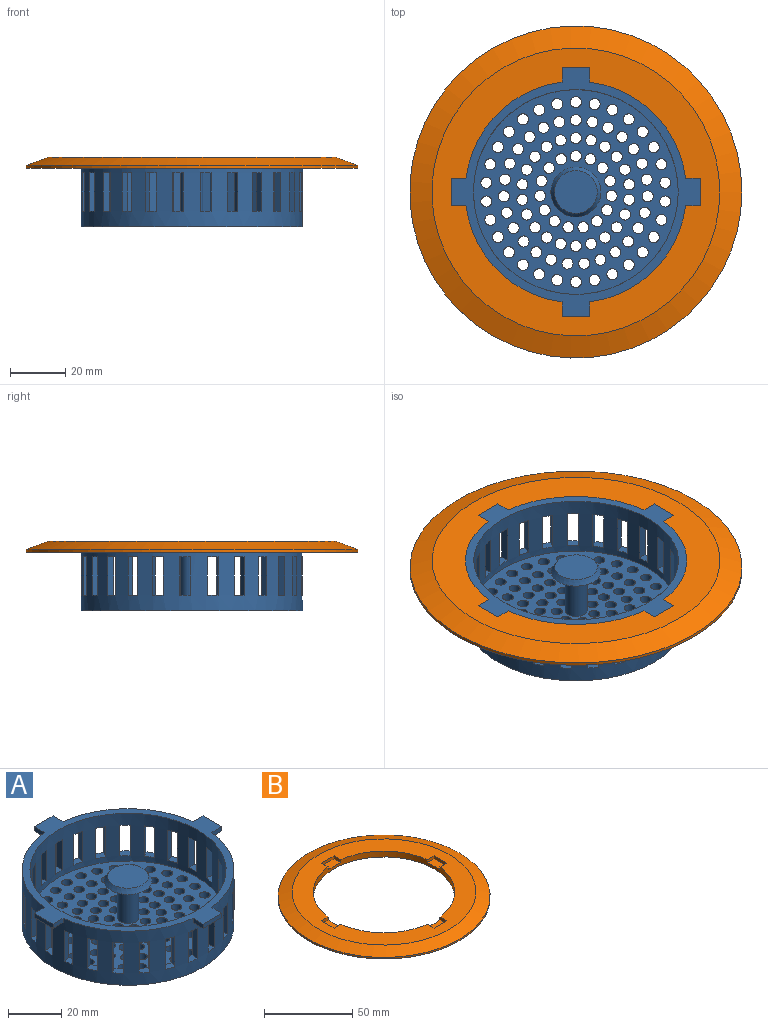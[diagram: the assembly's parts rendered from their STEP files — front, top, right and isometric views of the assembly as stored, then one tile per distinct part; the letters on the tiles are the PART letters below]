
ASSEMBLY  parts=2 mates=1
PART A: 226 faces, bbox 90x90x25 mm
  f0: cylinder r=40mm len=80mm, axis (0,0,-1), area 4802.4mm2, adj f2,f3,f5,f6,f8,f9,f10,f12
  f1: cylinder r=37mm len=74mm, axis (0,0,-1), area 3713.8mm2, adj f2,f4,f126,f127,f128,f129,f130,f131
  f2: plane 90x90mm, normal (0,0,1), area 929.9mm2, adj f0,f1,f5,f6,f7,f9,f10,f11
  f3: plane 80x80mm, normal (0,0,-1), area 3757.3mm2, adj f0,f21,f22,f23,f24,f25,f26,f27
  f4: plane 74x74mm, normal (0,0,1), area 2981.4mm2, adj f1,f21,f22,f23,f24,f25,f26,f27
  f5: plane 5.31x2mm, normal (-1,0,0), area 10.6mm2, adj f0,f2,f7,f8
  f6: plane 5.31x2mm, normal (1,0,0), area 10.6mm2, adj f0,f2,f7,f8
  f7: plane 10x2mm, normal (0,1,0), area 20mm2, adj f2,f5,f6,f8
  f8: plane 10x5.31mm, normal (0,0,-1), area 51mm2, adj f0,f5,f6,f7
  f9: plane 5.31x2mm, normal (0,-1,0), area 10.6mm2, adj f0,f2,f11,f12
  f10: plane 5.31x2mm, normal (0,1,0), area 10.6mm2, adj f0,f2,f11,f12
  f11: plane 10x2mm, normal (-1,0,0), area 20mm2, adj f2,f9,f10,f12
  f12: plane 10x5.31mm, normal (0,0,-1), area 51mm2, adj f0,f9,f10,f11
  f13: plane 5.31x2mm, normal (1,0,0), area 10.6mm2, adj f0,f2,f15,f16
  f14: plane 5.31x2mm, normal (-1,0,0), area 10.6mm2, adj f0,f2,f15,f16
  f15: plane 10x2mm, normal (0,-1,0), area 20mm2, adj f2,f13,f14,f16
  f16: plane 10x5.31mm, normal (0,0,-1), area 51mm2, adj f0,f13,f14,f15
  f17: plane 5.31x2mm, normal (0,1,0), area 10.6mm2, adj f0,f2,f19,f20
  f18: plane 5.31x2mm, normal (0,-1,0), area 10.6mm2, adj f0,f2,f19,f20
  f19: plane 10x2mm, normal (1,0,0), area 20mm2, adj f2,f17,f18,f20
  f20: plane 10x5.31mm, normal (0,0,-1), area 51mm2, adj f0,f17,f18,f19
  f21: cylinder r=2mm len=4mm, axis (0,0,1), area 37.7mm2, adj f3,f4
  f22: cylinder r=2mm len=4mm, axis (0,0,1), area 37.7mm2, adj f3,f4
  f23: cylinder r=2mm len=4mm, axis (0,0,1), area 37.7mm2, adj f3,f4
  f24: cylinder r=2mm len=4mm, axis (0,0,1), area 37.7mm2, adj f3,f4
  f25: cylinder r=2mm len=4mm, axis (0,0,1), area 37.7mm2, adj f3,f4
  f26: cylinder r=2mm len=4mm, axis (0,0,1), area 37.7mm2, adj f3,f4
  f27: cylinder r=2mm len=4mm, axis (0,0,1), area 37.7mm2, adj f3,f4
  f28: cylinder r=2mm len=4mm, axis (0,0,1), area 37.7mm2, adj f3,f4
  f29: cylinder r=2mm len=4mm, axis (0,0,1), area 37.7mm2, adj f3,f4
  f30: cylinder r=2mm len=4mm, axis (0,0,1), area 37.7mm2, adj f3,f4
  f31: cylinder r=2mm len=4mm, axis (0,0,1), area 37.7mm2, adj f3,f4
  f32: cylinder r=2mm len=4mm, axis (0,0,1), area 37.7mm2, adj f3,f4
  f33: cylinder r=2mm len=4mm, axis (0,0,1), area 37.7mm2, adj f3,f4
  f34: cylinder r=2mm len=4mm, axis (0,0,1), area 37.7mm2, adj f3,f4
  f35: cylinder r=2mm len=4mm, axis (0,0,1), area 37.7mm2, adj f3,f4
  f36: cylinder r=2mm len=4mm, axis (0,0,1), area 37.7mm2, adj f3,f4
  f37: cylinder r=2mm len=4mm, axis (0,0,1), area 37.7mm2, adj f3,f4
  f38: cylinder r=2mm len=4mm, axis (0,0,1), area 37.7mm2, adj f3,f4
  f39: cylinder r=2mm len=4mm, axis (0,0,1), area 37.7mm2, adj f3,f4
  f40: cylinder r=2mm len=4mm, axis (0,0,1), area 37.7mm2, adj f3,f4
  f41: cylinder r=2mm len=4mm, axis (0,0,1), area 37.7mm2, adj f3,f4
  f42: cylinder r=2mm len=4mm, axis (0,0,1), area 37.7mm2, adj f3,f4
  f43: cylinder r=2mm len=4mm, axis (0,0,1), area 37.7mm2, adj f3,f4
  f44: cylinder r=2mm len=4mm, axis (0,0,1), area 37.7mm2, adj f3,f4
  f45: cylinder r=2mm len=4mm, axis (0,0,1), area 37.7mm2, adj f3,f4
  f46: cylinder r=2mm len=4mm, axis (0,0,1), area 37.7mm2, adj f3,f4
  f47: cylinder r=2mm len=4mm, axis (0,0,1), area 37.7mm2, adj f3,f4
  f48: cylinder r=2mm len=4mm, axis (0,0,1), area 37.7mm2, adj f3,f4
  f49: cylinder r=2mm len=4mm, axis (0,0,1), area 37.7mm2, adj f3,f4
  f50: cylinder r=2mm len=4mm, axis (0,0,1), area 37.7mm2, adj f3,f4
  f51: cylinder r=2mm len=4mm, axis (0,0,1), area 37.7mm2, adj f3,f4
  f52: cylinder r=2mm len=4mm, axis (0,0,1), area 37.7mm2, adj f3,f4
  f53: cylinder r=2mm len=4mm, axis (0,0,1), area 37.7mm2, adj f3,f4
  f54: cylinder r=2mm len=4mm, axis (0,0,1), area 37.7mm2, adj f3,f4
  f55: cylinder r=2mm len=4mm, axis (0,0,1), area 37.7mm2, adj f3,f4
  f56: cylinder r=2mm len=4mm, axis (0,0,1), area 37.7mm2, adj f3,f4
  f57: cylinder r=2mm len=4mm, axis (0,0,1), area 37.7mm2, adj f3,f4
  f58: cylinder r=2mm len=4mm, axis (0,0,1), area 37.7mm2, adj f3,f4
  f59: cylinder r=2mm len=4mm, axis (0,0,1), area 37.7mm2, adj f3,f4
  f60: cylinder r=2mm len=4mm, axis (0,0,1), area 37.7mm2, adj f3,f4
  f61: cylinder r=2mm len=4mm, axis (0,0,1), area 37.7mm2, adj f3,f4
  f62: cylinder r=2mm len=4mm, axis (0,0,1), area 37.7mm2, adj f3,f4
  f63: cylinder r=2mm len=4mm, axis (0,0,1), area 37.7mm2, adj f3,f4
  f64: cylinder r=2mm len=4mm, axis (0,0,1), area 37.7mm2, adj f3,f4
  f65: cylinder r=2mm len=4mm, axis (0,0,1), area 37.7mm2, adj f3,f4
  f66: cylinder r=2mm len=4mm, axis (0,0,1), area 37.7mm2, adj f3,f4
  f67: cylinder r=2mm len=4mm, axis (0,0,1), area 37.7mm2, adj f3,f4
  f68: cylinder r=2mm len=4mm, axis (0,0,1), area 37.7mm2, adj f3,f4
  f69: cylinder r=2mm len=4mm, axis (0,0,1), area 37.7mm2, adj f3,f4
  f70: cylinder r=2mm len=4mm, axis (0,0,1), area 37.7mm2, adj f3,f4
  f71: cylinder r=2mm len=4mm, axis (0,0,1), area 37.7mm2, adj f3,f4
  f72: cylinder r=2mm len=4mm, axis (0,0,1), area 37.7mm2, adj f3,f4
  f73: cylinder r=2mm len=4mm, axis (0,0,1), area 37.7mm2, adj f3,f4
  f74: cylinder r=2mm len=4mm, axis (0,0,1), area 37.7mm2, adj f3,f4
  f75: cylinder r=2mm len=4mm, axis (0,0,1), area 37.7mm2, adj f3,f4
  f76: cylinder r=2mm len=4mm, axis (0,0,1), area 37.7mm2, adj f3,f4
  f77: cylinder r=2mm len=4mm, axis (0,0,1), area 37.7mm2, adj f3,f4
  f78: cylinder r=2mm len=4mm, axis (0,0,1), area 37.7mm2, adj f3,f4
  f79: cylinder r=2mm len=4mm, axis (0,0,1), area 37.7mm2, adj f3,f4
  f80: cylinder r=2mm len=4mm, axis (0,0,1), area 37.7mm2, adj f3,f4
  f81: cylinder r=2mm len=4mm, axis (0,0,1), area 37.7mm2, adj f3,f4
  f82: cylinder r=2mm len=4mm, axis (0,0,1), area 37.7mm2, adj f3,f4
  f83: cylinder r=2mm len=4mm, axis (0,0,1), area 37.7mm2, adj f3,f4
  f84: cylinder r=2mm len=4mm, axis (0,0,1), area 37.7mm2, adj f3,f4
  f85: cylinder r=2mm len=4mm, axis (0,0,1), area 37.7mm2, adj f3,f4
  f86: cylinder r=2mm len=4mm, axis (0,0,1), area 37.7mm2, adj f3,f4
  f87: cylinder r=2mm len=4mm, axis (0,0,1), area 37.7mm2, adj f3,f4
  f88: cylinder r=2mm len=4mm, axis (0,0,1), area 37.7mm2, adj f3,f4
  f89: cylinder r=2mm len=4mm, axis (0,0,1), area 37.7mm2, adj f3,f4
  f90: cylinder r=2mm len=4mm, axis (0,0,1), area 37.7mm2, adj f3,f4
  f91: cylinder r=2mm len=4mm, axis (0,0,1), area 37.7mm2, adj f3,f4
  f92: cylinder r=2mm len=4mm, axis (0,0,1), area 37.7mm2, adj f3,f4
  f93: cylinder r=2mm len=4mm, axis (0,0,1), area 37.7mm2, adj f3,f4
  f94: cylinder r=2mm len=4mm, axis (0,0,1), area 37.7mm2, adj f3,f4
  f95: cylinder r=2mm len=4mm, axis (0,0,1), area 37.7mm2, adj f3,f4
  f96: cylinder r=2mm len=4mm, axis (0,0,1), area 37.7mm2, adj f3,f4
  f97: cylinder r=2mm len=4mm, axis (0,0,1), area 37.7mm2, adj f3,f4
  f98: cylinder r=2mm len=4mm, axis (0,0,1), area 37.7mm2, adj f3,f4
  f99: cylinder r=2mm len=4mm, axis (0,0,1), area 37.7mm2, adj f3,f4
  f100: cylinder r=2mm len=4mm, axis (0,0,1), area 37.7mm2, adj f3,f4
  f101: cylinder r=2mm len=4mm, axis (0,0,1), area 37.7mm2, adj f3,f4
  f102: cylinder r=2mm len=4mm, axis (0,0,1), area 37.7mm2, adj f3,f4
  f103: cylinder r=2mm len=4mm, axis (0,0,1), area 37.7mm2, adj f3,f4
  f104: cylinder r=2mm len=4mm, axis (0,0,1), area 37.7mm2, adj f3,f4
  f105: cylinder r=2mm len=4mm, axis (0,0,1), area 37.7mm2, adj f3,f4
  f106: cylinder r=2mm len=4mm, axis (0,0,1), area 37.7mm2, adj f3,f4
  f107: cylinder r=2mm len=4mm, axis (0,0,1), area 37.7mm2, adj f3,f4
  f108: cylinder r=2mm len=4mm, axis (0,0,1), area 37.7mm2, adj f3,f4
  f109: cylinder r=2mm len=4mm, axis (0,0,1), area 37.7mm2, adj f3,f4
  f110: cylinder r=2mm len=4mm, axis (0,0,1), area 37.7mm2, adj f3,f4
  f111: cylinder r=2mm len=4mm, axis (0,0,1), area 37.7mm2, adj f3,f4
  f112: cylinder r=2mm len=4mm, axis (0,0,1), area 37.7mm2, adj f3,f4
  f113: cylinder r=2mm len=4mm, axis (0,0,1), area 37.7mm2, adj f3,f4
  f114: cylinder r=2mm len=4mm, axis (0,0,1), area 37.7mm2, adj f3,f4
  f115: cylinder r=2mm len=4mm, axis (0,0,1), area 37.7mm2, adj f3,f4
  f116: cylinder r=2mm len=4mm, axis (0,0,1), area 37.7mm2, adj f3,f4
  f117: cylinder r=2mm len=4mm, axis (0,0,1), area 37.7mm2, adj f3,f4
  f118: cylinder r=2mm len=4mm, axis (0,0,1), area 37.7mm2, adj f3,f4
  f119: cylinder r=2mm len=4mm, axis (0,0,1), area 37.7mm2, adj f3,f4
  f120: cylinder r=2mm len=4mm, axis (0,0,1), area 37.7mm2, adj f3,f4
  f121: cylinder r=2mm len=4mm, axis (0,0,1), area 37.7mm2, adj f3,f4
  f122: cylinder r=4mm len=17mm, axis (0,0,1), area 427.3mm2, adj f4,f123
  f123: plane 18x18mm, normal (0,0,-1), area 204.2mm2, adj f122,f124
  f124: cone r=9mm half-angle=32.8deg, axis (0,0,-1), area 124.9mm2, adj f123,f125
  f125: plane 15.42x15.42mm, normal (0,0,1), area 186.8mm2, adj f124
  f126: plane 14x2.98mm, normal (0.99,-0.13,0), area 42.1mm2, adj f0,f1,f128,f129
  f127: plane 14x2.98mm, normal (-0.99,0.13,0), area 42.1mm2, adj f0,f1,f128,f129
  f128: plane 4.35x3.48mm, normal (0,0,1), area 12mm2, adj f0,f1,f126,f127
  f129: plane 4.35x3.48mm, normal (0,0,-1), area 12mm2, adj f0,f1,f126,f127
  f130: plane 14x2.19mm, normal (-0.73,0.68,0), area 42.1mm2, adj f0,f1,f132,f133
  f131: plane 14x2.19mm, normal (0.73,-0.68,0), area 42.1mm2, adj f0,f1,f132,f133
  f132: plane 4.97x4.93mm, normal (0,0,1), area 12mm2, adj f0,f1,f130,f131
  f133: plane 4.97x4.93mm, normal (0,0,-1), area 12mm2, adj f0,f1,f130,f131
  f134: plane 14x3mm, normal (-0.06,1,0), area 42.1mm2, adj f0,f1,f136,f137
  f135: plane 14x3mm, normal (0.06,-1,0), area 42.1mm2, adj f0,f1,f136,f137
  f136: plane 4.18x3.25mm, normal (0,0,1), area 12mm2, adj f0,f1,f134,f135
  f137: plane 4.18x3.25mm, normal (0,0,-1), area 12mm2, adj f0,f1,f134,f135
  f138: plane 14x2.72mm, normal (0.43,-0.9,0), area 42.1mm2, adj f0,f1,f140,f141
  f139: plane 14x2.72mm, normal (-0.43,0.9,0), area 42.1mm2, adj f0,f1,f140,f141
  f140: plane 4.9x4.42mm, normal (0,0,1), area 12mm2, adj f0,f1,f138,f139
  f141: plane 4.9x4.42mm, normal (0,0,-1), area 12mm2, adj f0,f1,f138,f139
  f142: plane 14x2.95mm, normal (0.19,-0.98,0), area 42.1mm2, adj f0,f1,f144,f145
  f143: plane 14x2.95mm, normal (-0.19,0.98,0), area 42.1mm2, adj f0,f1,f144,f145
  f144: plane 4.49x3.7mm, normal (0,0,1), area 12mm2, adj f0,f1,f142,f143
  f145: plane 4.49x3.7mm, normal (0,0,-1), area 12mm2, adj f0,f1,f142,f143
  f146: plane 14x2.72mm, normal (0.43,0.9,0), area 42.1mm2, adj f0,f1,f148,f149
  f147: plane 14x2.72mm, normal (-0.43,-0.9,0), area 42.1mm2, adj f0,f1,f148,f149
  f148: plane 4.9x4.42mm, normal (0,0,1), area 12mm2, adj f0,f1,f146,f147
  f149: plane 4.9x4.42mm, normal (0,0,-1), area 12mm2, adj f0,f1,f146,f147
  f150: plane 14x2.95mm, normal (0.19,0.98,0), area 42.1mm2, adj f0,f1,f152,f153
  f151: plane 14x2.95mm, normal (-0.19,-0.98,0), area 42.1mm2, adj f0,f1,f152,f153
  f152: plane 4.49x3.7mm, normal (0,0,1), area 12mm2, adj f0,f1,f150,f151
  f153: plane 4.49x3.7mm, normal (0,0,-1), area 12mm2, adj f0,f1,f150,f151
  f154: plane 14x2.86mm, normal (-0.31,0.95,0), area 42.1mm2, adj f0,f1,f156,f157
  f155: plane 14x2.86mm, normal (0.31,-0.95,0), area 42.1mm2, adj f0,f1,f156,f157
  f156: plane 4.73x4.09mm, normal (0,0,1), area 12mm2, adj f0,f1,f154,f155
  f157: plane 4.73x4.09mm, normal (0,0,-1), area 12mm2, adj f0,f1,f154,f155
  f158: plane 14x2.31mm, normal (0.64,-0.77,0), area 42.1mm2, adj f0,f1,f160,f161
  f159: plane 14x2.31mm, normal (-0.64,0.77,0), area 42.1mm2, adj f0,f1,f160,f161
  f160: plane 5x4.86mm, normal (0,0,1), area 12mm2, adj f0,f1,f158,f159
  f161: plane 5x4.86mm, normal (0,0,-1), area 12mm2, adj f0,f1,f158,f159
  f162: plane 14x2.31mm, normal (0.64,0.77,0), area 42.1mm2, adj f0,f1,f164,f165
  f163: plane 14x2.31mm, normal (-0.64,-0.77,0), area 42.1mm2, adj f0,f1,f164,f165
  f164: plane 5x4.86mm, normal (0,0,1), area 12mm2, adj f0,f1,f162,f163
  f165: plane 5x4.86mm, normal (0,0,-1), area 12mm2, adj f0,f1,f162,f163
  f166: plane 14x2.43mm, normal (0.81,0.59,0), area 42.1mm2, adj f0,f1,f168,f169
  f167: plane 14x2.43mm, normal (-0.81,-0.59,0), area 42.1mm2, adj f0,f1,f168,f169
  f168: plane 5x4.78mm, normal (0,0,1), area 12mm2, adj f0,f1,f166,f167
  f169: plane 5x4.78mm, normal (0,0,-1), area 12mm2, adj f0,f1,f166,f167
  f170: plane 14x2.63mm, normal (-0.88,0.48,0), area 42.1mm2, adj f0,f1,f172,f173
  f171: plane 14x2.63mm, normal (0.88,-0.48,0), area 42.1mm2, adj f0,f1,f172,f173
  f172: plane 4.95x4.56mm, normal (0,0,1), area 12mm2, adj f0,f1,f170,f171
  f173: plane 4.95x4.56mm, normal (0,0,-1), area 12mm2, adj f0,f1,f170,f171
  f174: plane 14x2.98mm, normal (0.99,0.13,0), area 42.1mm2, adj f0,f1,f176,f177
  f175: plane 14x2.98mm, normal (-0.99,-0.13,0), area 42.1mm2, adj f0,f1,f176,f177
  f176: plane 4.35x3.48mm, normal (0,0,1), area 12mm2, adj f0,f1,f174,f175
  f177: plane 4.35x3.48mm, normal (0,0,-1), area 12mm2, adj f0,f1,f174,f175
  f178: plane 14x3mm, normal (-1,0,0), area 42.1mm2, adj f0,f1,f180,f181
  f179: plane 14x3mm, normal (1,0,0), area 42.1mm2, adj f0,f1,f180,f181
  f180: plane 4x3.05mm, normal (0,0,1), area 12mm2, adj f0,f1,f178,f179
  f181: plane 4x3.05mm, normal (0,0,-1), area 12mm2, adj f0,f1,f178,f179
  f182: plane 14x2.63mm, normal (-0.88,-0.48,0), area 42.1mm2, adj f0,f1,f184,f185
  f183: plane 14x2.63mm, normal (0.88,0.48,0), area 42.1mm2, adj f0,f1,f184,f185
  f184: plane 4.95x4.56mm, normal (0,0,1), area 12mm2, adj f0,f1,f182,f183
  f185: plane 4.95x4.56mm, normal (0,0,-1), area 12mm2, adj f0,f1,f182,f183
  f186: plane 14x2.79mm, normal (0.93,0.37,0), area 42.1mm2, adj f0,f1,f188,f189
  f187: plane 14x2.79mm, normal (-0.93,-0.37,0), area 42.1mm2, adj f0,f1,f188,f189
  f188: plane 4.83x4.27mm, normal (0,0,1), area 12mm2, adj f0,f1,f186,f187
  f189: plane 4.83x4.27mm, normal (0,0,-1), area 12mm2, adj f0,f1,f186,f187
  f190: plane 14x2.19mm, normal (-0.73,-0.68,0), area 42.1mm2, adj f0,f1,f192,f193
  f191: plane 14x2.19mm, normal (0.73,0.68,0), area 42.1mm2, adj f0,f1,f192,f193
  f192: plane 4.97x4.93mm, normal (0,0,1), area 12mm2, adj f0,f1,f190,f191
  f193: plane 4.97x4.93mm, normal (0,0,-1), area 12mm2, adj f0,f1,f190,f191
  f194: plane 14x2.86mm, normal (-0.31,-0.95,0), area 42.1mm2, adj f0,f1,f196,f197
  f195: plane 14x2.86mm, normal (0.31,0.95,0), area 42.1mm2, adj f0,f1,f196,f197
  f196: plane 4.73x4.09mm, normal (0,0,1), area 12mm2, adj f0,f1,f194,f195
  f197: plane 4.73x4.09mm, normal (0,0,-1), area 12mm2, adj f0,f1,f194,f195
  f198: plane 14x2.91mm, normal (-0.97,-0.25,0), area 42.1mm2, adj f0,f1,f200,f201
  f199: plane 14x2.91mm, normal (0.97,0.25,0), area 42.1mm2, adj f0,f1,f200,f201
  f200: plane 4.62x3.9mm, normal (0,0,1), area 12mm2, adj f0,f1,f198,f199
  f201: plane 4.62x3.9mm, normal (0,0,-1), area 12mm2, adj f0,f1,f198,f199
  f202: plane 14x2.79mm, normal (0.93,-0.37,0), area 42.1mm2, adj f0,f1,f204,f205
  f203: plane 14x2.79mm, normal (-0.93,0.37,0), area 42.1mm2, adj f0,f1,f204,f205
  f204: plane 4.83x4.27mm, normal (0,0,1), area 12mm2, adj f0,f1,f202,f203
  f205: plane 4.83x4.27mm, normal (0,0,-1), area 12mm2, adj f0,f1,f202,f203
  f206: plane 14x2.43mm, normal (0.81,-0.59,0), area 42.1mm2, adj f0,f1,f208,f209
  f207: plane 14x2.43mm, normal (-0.81,0.59,0), area 42.1mm2, adj f0,f1,f208,f209
  f208: plane 5x4.78mm, normal (0,0,1), area 12mm2, adj f0,f1,f206,f207
  f209: plane 5x4.78mm, normal (0,0,-1), area 12mm2, adj f0,f1,f206,f207
  f210: plane 14x2.54mm, normal (-0.54,0.84,0), area 42.1mm2, adj f0,f1,f212,f213
  f211: plane 14x2.54mm, normal (0.54,-0.84,0), area 42.1mm2, adj f0,f1,f212,f213
  f212: plane 4.99x4.68mm, normal (0,0,1), area 12mm2, adj f0,f1,f210,f211
  f213: plane 4.99x4.68mm, normal (0,0,-1), area 12mm2, adj f0,f1,f210,f211
  f214: plane 14x2.54mm, normal (-0.54,-0.84,0), area 42.1mm2, adj f0,f1,f216,f217
  f215: plane 14x2.54mm, normal (0.54,0.84,0), area 42.1mm2, adj f0,f1,f216,f217
  f216: plane 4.99x4.68mm, normal (0,0,1), area 12mm2, adj f0,f1,f214,f215
  f217: plane 4.99x4.68mm, normal (0,0,-1), area 12mm2, adj f0,f1,f214,f215
  f218: plane 14x3mm, normal (-0.06,-1,0), area 42.1mm2, adj f0,f1,f220,f221
  f219: plane 14x3mm, normal (0.06,1,0), area 42.1mm2, adj f0,f1,f220,f221
  f220: plane 4.18x3.25mm, normal (0,0,1), area 12mm2, adj f0,f1,f218,f219
  f221: plane 4.18x3.25mm, normal (0,0,-1), area 12mm2, adj f0,f1,f218,f219
  f222: plane 14x2.91mm, normal (-0.97,0.25,0), area 42.1mm2, adj f0,f1,f224,f225
  f223: plane 14x2.91mm, normal (0.97,-0.25,0), area 42.1mm2, adj f0,f1,f224,f225
  f224: plane 4.62x3.9mm, normal (0,0,1), area 12mm2, adj f0,f1,f222,f223
  f225: plane 4.62x3.9mm, normal (0,0,-1), area 12mm2, adj f0,f1,f222,f223
PART B: 21 faces, bbox 120x120x4 mm
  f0: plane 104x104mm, normal (0,0,1), area 3264.1mm2, adj f1,f4,f5,f6,f8,f9,f10,f12
  f1: cylinder r=40mm len=80mm, axis (0,0,1), area 925.1mm2, adj f0,f3,f4,f5,f7,f8,f9,f11
  f2: cylinder r=60mm len=120mm, axis (0,0,1), area 410.3mm2, adj f3,f20
  f3: plane 120x120mm, normal (0,0,-1), area 6283.2mm2, adj f1,f2
  f4: plane 5.31x2mm, normal (0,1,0), area 10.6mm2, adj f0,f1,f6,f7
  f5: plane 5.31x2mm, normal (0,-1,0), area 10.6mm2, adj f0,f1,f6,f7
  f6: plane 10x2mm, normal (1,0,0), area 20mm2, adj f0,f4,f5,f7
  f7: plane 10x5.31mm, normal (0,0,1), area 51mm2, adj f1,f4,f5,f6
  f8: plane 5.31x2mm, normal (-1,0,0), area 10.6mm2, adj f0,f1,f10,f11
  f9: plane 5.31x2mm, normal (1,0,0), area 10.6mm2, adj f0,f1,f10,f11
  f10: plane 10x2mm, normal (0,1,0), area 20mm2, adj f0,f8,f9,f11
  f11: plane 10x5.31mm, normal (0,0,1), area 51mm2, adj f1,f8,f9,f10
  f12: plane 5.31x2mm, normal (0,-1,0), area 10.6mm2, adj f0,f1,f14,f15
  f13: plane 5.31x2mm, normal (0,1,0), area 10.6mm2, adj f0,f1,f14,f15
  f14: plane 10x2mm, normal (-1,0,0), area 20mm2, adj f0,f12,f13,f15
  f15: plane 10x5.31mm, normal (0,0,1), area 51mm2, adj f1,f12,f13,f14
  f16: plane 5.31x2mm, normal (1,0,0), area 10.6mm2, adj f0,f1,f18,f19
  f17: plane 5.31x2mm, normal (-1,0,0), area 10.6mm2, adj f0,f1,f18,f19
  f18: plane 10x2mm, normal (0,-1,0), area 20mm2, adj f0,f16,f17,f19
  f19: plane 10x5.31mm, normal (0,0,1), area 51mm2, adj f1,f16,f17,f18
  f20: cone r=52mm half-angle=70deg, axis (0,0,-1), area 2995.5mm2, adj f0,f2
PLACE A at identity
PLACE B at identity fixed
MATE slider B.f7 <-> A.f12  axis (0,0,1) through (-42.45,0,23)mm
